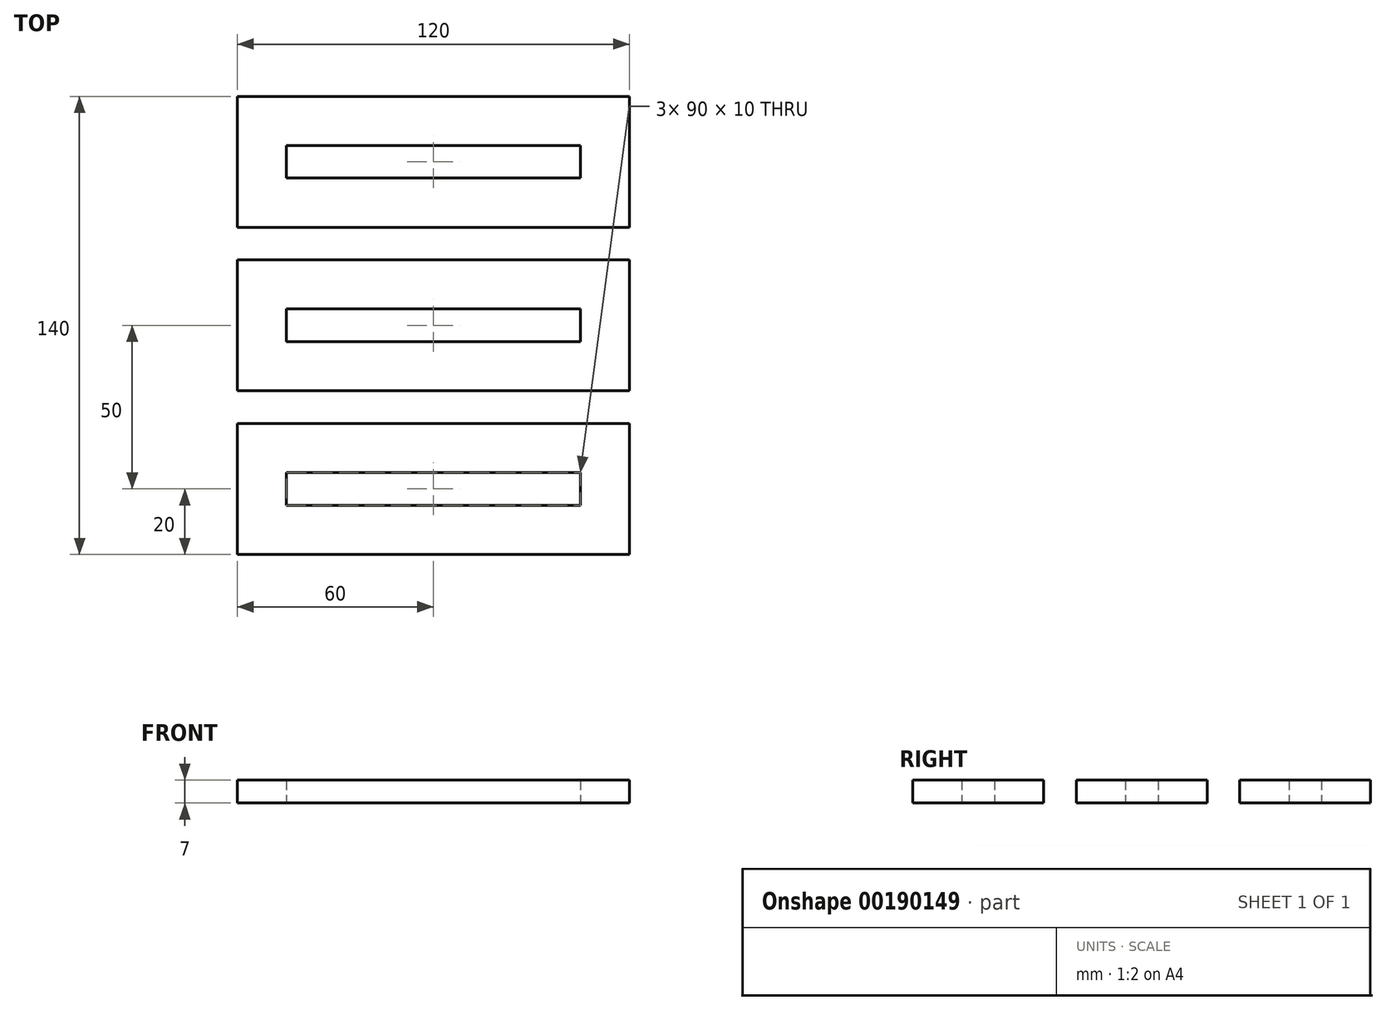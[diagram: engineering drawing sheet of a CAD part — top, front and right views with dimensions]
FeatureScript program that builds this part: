
annotation { "Feature Type Name" : "Feature", "Feature Type Description" : "" }
export const myFeature = defineFeature(function(context is Context, id is Id, definition is map)
    precondition{}
    {
        {
            var Q0;
            Q0=qCreatedBy(makeId("Top.planeOp"),FACE);
            var sketch = newSketch(context, id + "F0", { "sketchPlane" : qUnion([Q0])});
            skLineSegment(sketch, "E0.bottom", {"start": v(60, -20) * mm, "end": v(-60, -20) * mm});
            skLineSegment(sketch, "E0.top", {"start": v(60, 20) * mm, "end": v(-60, 20) * mm});
            skLineSegment(sketch, "E0.left", {"start": v(60, -20) * mm, "end": v(60, 20) * mm});
            skLineSegment(sketch, "E0.right", {"start": v(-60, -20) * mm, "end": v(-60, 20) * mm});
            skPoint(sketch, "E0.middle", {"position": v(0, 0) * mm});
            skLineSegment(sketch, "E1.0", {"start": v(45, -5) * mm, "end": v(45, 5) * mm});
            skLineSegment(sketch, "E1.1", {"start": v(45, -5) * mm, "end": v(-45, -5) * mm});
            skLineSegment(sketch, "E1.2", {"start": v(-45, -5) * mm, "end": v(-45, 5) * mm});
            skLineSegment(sketch, "E1.3", {"start": v(45, 5) * mm, "end": v(-45, 5) * mm});
            skLineSegment(sketch, "E2.0.1.0", {"start": v(60, 30) * mm, "end": v(60, 70) * mm});
            skLineSegment(sketch, "E2.0.1.1", {"start": v(45, 45) * mm, "end": v(-45, 45) * mm});
            skLineSegment(sketch, "E2.0.1.2", {"start": v(-45, 45) * mm, "end": v(-45, 55) * mm});
            skLineSegment(sketch, "E2.0.1.3", {"start": v(60, 30) * mm, "end": v(-60, 30) * mm});
            skLineSegment(sketch, "E2.0.1.4", {"start": v(45, 55) * mm, "end": v(-45, 55) * mm});
            skLineSegment(sketch, "E2.0.1.5", {"start": v(-60, 30) * mm, "end": v(-60, 70) * mm});
            skLineSegment(sketch, "E2.0.1.6", {"start": v(45, 45) * mm, "end": v(45, 55) * mm});
            skLineSegment(sketch, "E2.0.1.7", {"start": v(60, 70) * mm, "end": v(-60, 70) * mm});
            skPoint(sketch, "E2.0.1.8", {"position": v(0, 50) * mm});
            skLineSegment(sketch, "E2.0.2.0", {"start": v(60, 80) * mm, "end": v(60, 120) * mm});
            skLineSegment(sketch, "E2.0.2.1", {"start": v(45, 95) * mm, "end": v(-45, 95) * mm});
            skLineSegment(sketch, "E2.0.2.2", {"start": v(-45, 95) * mm, "end": v(-45, 105) * mm});
            skLineSegment(sketch, "E2.0.2.3", {"start": v(60, 80) * mm, "end": v(-60, 80) * mm});
            skLineSegment(sketch, "E2.0.2.4", {"start": v(45, 105) * mm, "end": v(-45, 105) * mm});
            skLineSegment(sketch, "E2.0.2.5", {"start": v(-60, 80) * mm, "end": v(-60, 120) * mm});
            skLineSegment(sketch, "E2.0.2.6", {"start": v(45, 95) * mm, "end": v(45, 105) * mm});
            skLineSegment(sketch, "E2.0.2.7", {"start": v(60, 120) * mm, "end": v(-60, 120) * mm});
            skPoint(sketch, "E2.0.2.8", {"position": v(0, 100) * mm});
            skLineSegment(sketch, "E2.1.0.0", {"start": v(190, -20) * mm, "end": v(190, 20) * mm});
            skLineSegment(sketch, "E2.1.0.1", {"start": v(175, -5) * mm, "end": v(85, -5) * mm});
            skLineSegment(sketch, "E2.1.0.2", {"start": v(85, -5) * mm, "end": v(85, 5) * mm});
            skLineSegment(sketch, "E2.1.0.3", {"start": v(190, -20) * mm, "end": v(70, -20) * mm});
            skLineSegment(sketch, "E2.1.0.4", {"start": v(175, 5) * mm, "end": v(85, 5) * mm});
            skLineSegment(sketch, "E2.1.0.5", {"start": v(70, -20) * mm, "end": v(70, 20) * mm});
            skLineSegment(sketch, "E2.1.0.6", {"start": v(175, -5) * mm, "end": v(175, 5) * mm});
            skLineSegment(sketch, "E2.1.0.7", {"start": v(190, 20) * mm, "end": v(70, 20) * mm});
            skPoint(sketch, "E2.1.0.8", {"position": v(130, 0) * mm});
            skLineSegment(sketch, "E2.1.1.0", {"start": v(190, 30) * mm, "end": v(190, 70) * mm});
            skLineSegment(sketch, "E2.1.1.1", {"start": v(175, 45) * mm, "end": v(85, 45) * mm});
            skLineSegment(sketch, "E2.1.1.2", {"start": v(85, 45) * mm, "end": v(85, 55) * mm});
            skLineSegment(sketch, "E2.1.1.3", {"start": v(190, 30) * mm, "end": v(70, 30) * mm});
            skLineSegment(sketch, "E2.1.1.4", {"start": v(175, 55) * mm, "end": v(85, 55) * mm});
            skLineSegment(sketch, "E2.1.1.5", {"start": v(70, 30) * mm, "end": v(70, 70) * mm});
            skLineSegment(sketch, "E2.1.1.6", {"start": v(175, 45) * mm, "end": v(175, 55) * mm});
            skLineSegment(sketch, "E2.1.1.7", {"start": v(190, 70) * mm, "end": v(70, 70) * mm});
            skPoint(sketch, "E2.1.1.8", {"position": v(130, 50) * mm});
            skLineSegment(sketch, "E2.1.2.0", {"start": v(190, 80) * mm, "end": v(190, 120) * mm});
            skLineSegment(sketch, "E2.1.2.1", {"start": v(175, 95) * mm, "end": v(85, 95) * mm});
            skLineSegment(sketch, "E2.1.2.2", {"start": v(85, 95) * mm, "end": v(85, 105) * mm});
            skLineSegment(sketch, "E2.1.2.3", {"start": v(190, 80) * mm, "end": v(70, 80) * mm});
            skLineSegment(sketch, "E2.1.2.4", {"start": v(175, 105) * mm, "end": v(85, 105) * mm});
            skLineSegment(sketch, "E2.1.2.5", {"start": v(70, 80) * mm, "end": v(70, 120) * mm});
            skLineSegment(sketch, "E2.1.2.6", {"start": v(175, 95) * mm, "end": v(175, 105) * mm});
            skLineSegment(sketch, "E2.1.2.7", {"start": v(190, 120) * mm, "end": v(70, 120) * mm});
            skPoint(sketch, "E2.1.2.8", {"position": v(130, 100) * mm});
            skLineSegment(sketch, "E2.direction1", {"start": v(-60, -20) * mm, "end": v(70, -20) * mm, "construction": true});
            skLineSegment(sketch, "E2.direction2", {"start": v(-60, -20) * mm, "end": v(-60, 30) * mm, "construction": true});
            skSolve(sketch);
        }
        {
            var Q0;
            Q0=qSketchRegion(id+"F0",true);
            extrude(context, id + "F1", {"entities" : qUnion([Q0]), "depth" : 7 * mm, "offsetDistance" : 25 * mm});
        }
        {
            var Q0;
            Q0=makeQuery(id+"F1.opExtrude","SWEPT_BODY",BODY,{"disambiguationData":[OSD([sQuery(id+"F0.wireOp",EDGE,"E0.bottom"),sQuery(id+"F0.wireOp",EDGE,"E0.top"),sQuery(id+"F0.wireOp",EDGE,"E0.left"),sQuery(id+"F0.wireOp",EDGE,"E0.right"),sQuery(id+"F0.wireOp",EDGE,"E1.0"),sQuery(id+"F0.wireOp",EDGE,"E1.1"),sQuery(id+"F0.wireOp",EDGE,"E1.2"),sQuery(id+"F0.wireOp",EDGE,"E1.3")])]});
            transform(context, id + "F2", {"entities" : qUnion([Q0]), "transformType" : TransformType.TRANSLATION_3D, "dx" : 0 * mm, "dy" : 90 * mm, "dz" : 0 * mm, "makeCopy" : true});
        }
        {
            var Q0;
            Q0=makeQuery(id+"F2.opPattern","COPY",BODY,{"derivedFrom":makeQuery(id+"F1.opExtrude","SWEPT_BODY",BODY,{"disambiguationData":[OSD([sQuery(id+"F0.wireOp",EDGE,"E0.bottom"),sQuery(id+"F0.wireOp",EDGE,"E0.top"),sQuery(id+"F0.wireOp",EDGE,"E0.left"),sQuery(id+"F0.wireOp",EDGE,"E0.right"),sQuery(id+"F0.wireOp",EDGE,"E1.0"),sQuery(id+"F0.wireOp",EDGE,"E1.1"),sQuery(id+"F0.wireOp",EDGE,"E1.2"),sQuery(id+"F0.wireOp",EDGE,"E1.3")])]}),"instanceName":"1"});
            transform(context, id + "F3", {"entities" : qUnion([Q0]), "transformType" : TransformType.TRANSLATION_3D, "dx" : 0 * mm, "dy" : 90 * mm, "dz" : 0 * mm, "makeCopy" : true});
        }
        {
            var Q0;
            Q0=makeQuery(id+"F3.opPattern","COPY",BODY,{"derivedFrom":makeQuery(id+"F2.opPattern","COPY",BODY,{"derivedFrom":makeQuery(id+"F1.opExtrude","SWEPT_BODY",BODY,{"disambiguationData":[OSD([sQuery(id+"F0.wireOp",EDGE,"E0.bottom"),sQuery(id+"F0.wireOp",EDGE,"E0.top"),sQuery(id+"F0.wireOp",EDGE,"E0.left"),sQuery(id+"F0.wireOp",EDGE,"E0.right"),sQuery(id+"F0.wireOp",EDGE,"E1.0"),sQuery(id+"F0.wireOp",EDGE,"E1.1"),sQuery(id+"F0.wireOp",EDGE,"E1.2"),sQuery(id+"F0.wireOp",EDGE,"E1.3")])]}),"instanceName":"1"}),"instanceName":"1"});
            deleteBodies(context, id + "F4", {"entities" : qUnion([Q0])});
        }
        {
            var Q0;
            Q0=makeQuery(id+"F2.opPattern","COPY",BODY,{"derivedFrom":makeQuery(id+"F1.opExtrude","SWEPT_BODY",BODY,{"disambiguationData":[OSD([sQuery(id+"F0.wireOp",EDGE,"E0.bottom"),sQuery(id+"F0.wireOp",EDGE,"E0.top"),sQuery(id+"F0.wireOp",EDGE,"E0.left"),sQuery(id+"F0.wireOp",EDGE,"E0.right"),sQuery(id+"F0.wireOp",EDGE,"E1.0"),sQuery(id+"F0.wireOp",EDGE,"E1.1"),sQuery(id+"F0.wireOp",EDGE,"E1.2"),sQuery(id+"F0.wireOp",EDGE,"E1.3")])]}),"instanceName":"1"});
            deleteBodies(context, id + "F5", {"entities" : qUnion([Q0])});
        }
        {
            var Q0;
            Q0=makeQuery(id+"F1.opExtrude","SWEPT_BODY",BODY,{"disambiguationData":[OSD([sQuery(id+"F0.wireOp",EDGE,"E2.1.2.0"),sQuery(id+"F0.wireOp",EDGE,"E2.1.2.1"),sQuery(id+"F0.wireOp",EDGE,"E2.1.2.2"),sQuery(id+"F0.wireOp",EDGE,"E2.1.2.3"),sQuery(id+"F0.wireOp",EDGE,"E2.1.2.4"),sQuery(id+"F0.wireOp",EDGE,"E2.1.2.5"),sQuery(id+"F0.wireOp",EDGE,"E2.1.2.6"),sQuery(id+"F0.wireOp",EDGE,"E2.1.2.7")])]});
            var Q1;
            Q1=makeQuery(id+"F1.opExtrude","SWEPT_BODY",BODY,{"disambiguationData":[OSD([sQuery(id+"F0.wireOp",EDGE,"E2.1.0.0"),sQuery(id+"F0.wireOp",EDGE,"E2.1.0.1"),sQuery(id+"F0.wireOp",EDGE,"E2.1.0.2"),sQuery(id+"F0.wireOp",EDGE,"E2.1.0.3"),sQuery(id+"F0.wireOp",EDGE,"E2.1.0.4"),sQuery(id+"F0.wireOp",EDGE,"E2.1.0.5"),sQuery(id+"F0.wireOp",EDGE,"E2.1.0.6"),sQuery(id+"F0.wireOp",EDGE,"E2.1.0.7")])]});
            var Q2;
            Q2=makeQuery(id+"F1.opExtrude","SWEPT_BODY",BODY,{"disambiguationData":[OSD([sQuery(id+"F0.wireOp",EDGE,"E2.1.1.0"),sQuery(id+"F0.wireOp",EDGE,"E2.1.1.1"),sQuery(id+"F0.wireOp",EDGE,"E2.1.1.2"),sQuery(id+"F0.wireOp",EDGE,"E2.1.1.3"),sQuery(id+"F0.wireOp",EDGE,"E2.1.1.4"),sQuery(id+"F0.wireOp",EDGE,"E2.1.1.5"),sQuery(id+"F0.wireOp",EDGE,"E2.1.1.6"),sQuery(id+"F0.wireOp",EDGE,"E2.1.1.7")])]});
            deleteBodies(context, id + "F6", {"entities" : qUnion([Q0, Q1, Q2])});
        }
    });
